# Revit family: ГРЕЕРС Д2
name_source: partatom
category: Обобщенные модели
revit_build: Autodesk Revit 2017 (Build: 20161006_0315(x64)
units: mm (PartAtom-declared; Revit-internal decimal feet)

## family parameters
Может служить основой для арматурных стержней = Нет
Общий = Нет
Основа = Грань
При загрузке вырезать с полостями = Нет
Размер круглого соединителя = Использовать диаметр
Тип детали = Нормальный
Точка расчета площади = Нет

## types (3) — shared parameters
URL = https://greers.ru
Вентилятор = Осевой, однофазный, переменного тока, с 3-х скоростным двигателем
Вес аппарата = 14.10 кг
Группа модели = ГРЕЕРС Д2
Изготовитель = ООО "ЮНИО-ВЕНТ"
Класс защиты = IP 54
Классификация нагрузки = Двигатель
Коэффициент мощности = 1
Максимальное потребление тока = 1 А
Материал = EPP
Напряжение питания = 230 В
Описание = Дестратификатор воздуха
Отметка по умолчанию = 800 мм
Расстояние до перекрытия = 800 мм

## per-type parameters (varying)
| type | Максимальный расход мощности | Полная установленная мощность | Производительность |
| ГРЕЕРС Д2 (1-я скорость) | 170 Вт | 179 В·А | 3500.0 м³/ч |
| ГРЕЕРС Д2 (2-я скорость) | 200 Вт | 202 В·А | 4500.0 м³/ч |
| ГРЕЕРС Д2 (3-я скорость) | 260 Вт | 276 В·А | 5400.0 м³/ч |
